# Revit family: Ball_Valve-NPT-Full_Port-WATTS-LFB6090_Series.rfaxxx
name_source: partatom
category: Pipe Accessories
units: mm (PartAtom-declared; Revit-internal decimal feet)

## family parameters
Always vertical = No
Cut with Voids When Loaded = No
OmniClass Number = 23.65.55.14
OmniClass Title = Valves for Liquid Services
Part Type = Valve - Breaks Into
Round Connector Dimension = Use Diameter
Shared = Yes
Work Plane-Based = Yes

## types (8) — shared parameters
Assembly Code = D2090900
Country = United States
Default Elevation = 0"
Description = 2-Piece, Full Port, Lead Free* Bronze Ball Valves
Finish = Metal-WATTS-Lead Free Bronze
Finish- Handle = Plastic-WATTS-White
LFB6090 NPT = Yes
LFB6091 Solder = No
Manufacturer = WATTS
Manufacturer Product Line = Ball Valves
Material = Metal-WATTS-Lead Free Bronze
Pressure Range = 1⁄4-in to 2-in 600psi (41 bar) WOG, non-shock; 150psi (10.3 bar) WSP
Price = Prices may vary. Please consult Manufacturer Representative for most up-to-date price list.
Product Documentation Link = https://www.watts.com
Product Page URL = https://www.watts.com
Region = North America
Temperature Range = 0°F - 400°F (-18°C – 205°C) @ 50psi (3.4 bar)
Tempered Water Connection = Yes
URL = http://www.watts.com

## per-type parameters (varying)
| type | Body Length | Bolt_Hex | C | Connection Diameter | H | Handle R | I | L | Locking Handle Kit | NPT Inlet Connection Description | NPT Outlet Connection Description | Stem Diameter | Stem Extension | Valve Diameter | Weight Lbs |
| 1/4 LFB6090 | 11/32" | 21/32" | 1 13/16" | 1/4" | 3 7/16" | 5/16" | 7/16" | 1 3/4" | #1 LL-HK LFB6090/LFB6091 1/4-1/2 LockingHandleKit | 1/4-in NPT Inlet Connection | 1/4-in NPT Outlet Connection | 5/8" | 1/4"-1/2" 6090/6091 | 1 1/8" | 0.4 |
| 3/8 LFB6090 | 3/8" | 3/4" | 1 13/16" | 3/8" | 3 7/16" | 5/16" | 1/2" | 1 7/8" | #1 LL-HK LFB6090/LFB6091 1/4-1/2 LockingHandleKit | 3/8-in NPT Inlet Connection | 3/8-in NPT Outlet Connection | 5/8" | 1/4"-1/2" 6090/6091 | 1 1/8" | 0.4 |
| 1/2 LFB6090 | 13/32" | 3/4" | 1 13/16" | 1/2" | 3 7/16" | 5/16" | 1/2" | 2" | #1 LL-HK LFB6090/LFB6091 1/4-1/2 LockingHandleKit | 1/2-in NPT Inlet Connection | 1/2-in NPT Outlet Connection | 5/8" | 1/4"-1/2" 6090/6091 | 1 1/8" | 0.5 |
| 3/4 LFB6090 | 7/16" | 1 1/8" | 2 1/4" | 3/4" | 3 15/16" | 3/8" | 3/4" | 2 1/4" | #2 LL-HK LFB6090/LFB6091 3/4 LockingHandleKit | 3/4-in NPT Inlet Connection | 3/4-in NPT Outlet Connection | 3/4" | SKI-HK-9A Stem Extension | 1 9/16" | 0.9 |
| 1 LFB6090 | 19/32" | 1 1/2" | 2 5/8" | 1" | 4 1/4" | 15/32" | 1" | 3" | #3 LL-HK LFB6090/LFB6091 1-1 1/4 LockingHandleKit | 1-in NPT Inlet Connection | 1-in NPT Outlet Connection | 15/16" | SKI-HK-10A Stem Extension | 1 13/16" | 1.4 |
| 1 1/4 LFB6090 | 11/16" | 1 7/8" | 2 13/16" | 1 1/4" | 4 1/4" | 15/32" | 1 1/4" | 3 3/8" | #3 LL-HK LFB6090/LFB6091 1-1 1/4 LockingHandleKit | 1 1/4-in NPT Inlet Connection | 1 1/4-in NPT Outlet Connection | 29/32" | SKI-HK-10A Stem Extension | 2 1/4" | 2.1 |
| 1 1/2 LFB6090 | 3/4" | 2 1/4" | 3 3/16" | 1 1/2" | 5 5/16" | 15/32" | 1 1/2" | 3 11/16" | #4 LL-HK LFB6090/LFB6091 1 1/2 LockingHandleKit | 1 1/2-in NPT Inlet Connection | 1 1/2-in NPT Outlet Connection | 31/32" | SKI-HK-11A Stem Extension | 2 21/32" | 3.1 |
| 2 LFB6090 | 27/32" | 3" | 3 1/2" | 2" | 6" | 15/32" | 2" | 4 1/4" | #5 LL-HK LFB6090/LFB6091 2 LockingHandleKit | 2-in NPT Inlet Connection | 2-in NPT Outlet Connection | 31/32" | SKI-HK-5A Stem Extension | 3 3/8" | 4.9 |

note: column(s) folded — value = type name in every type: Model

## geometry (parser evidence)
native form markers: Sweep x2
no freeform markers — native parametric forms only
